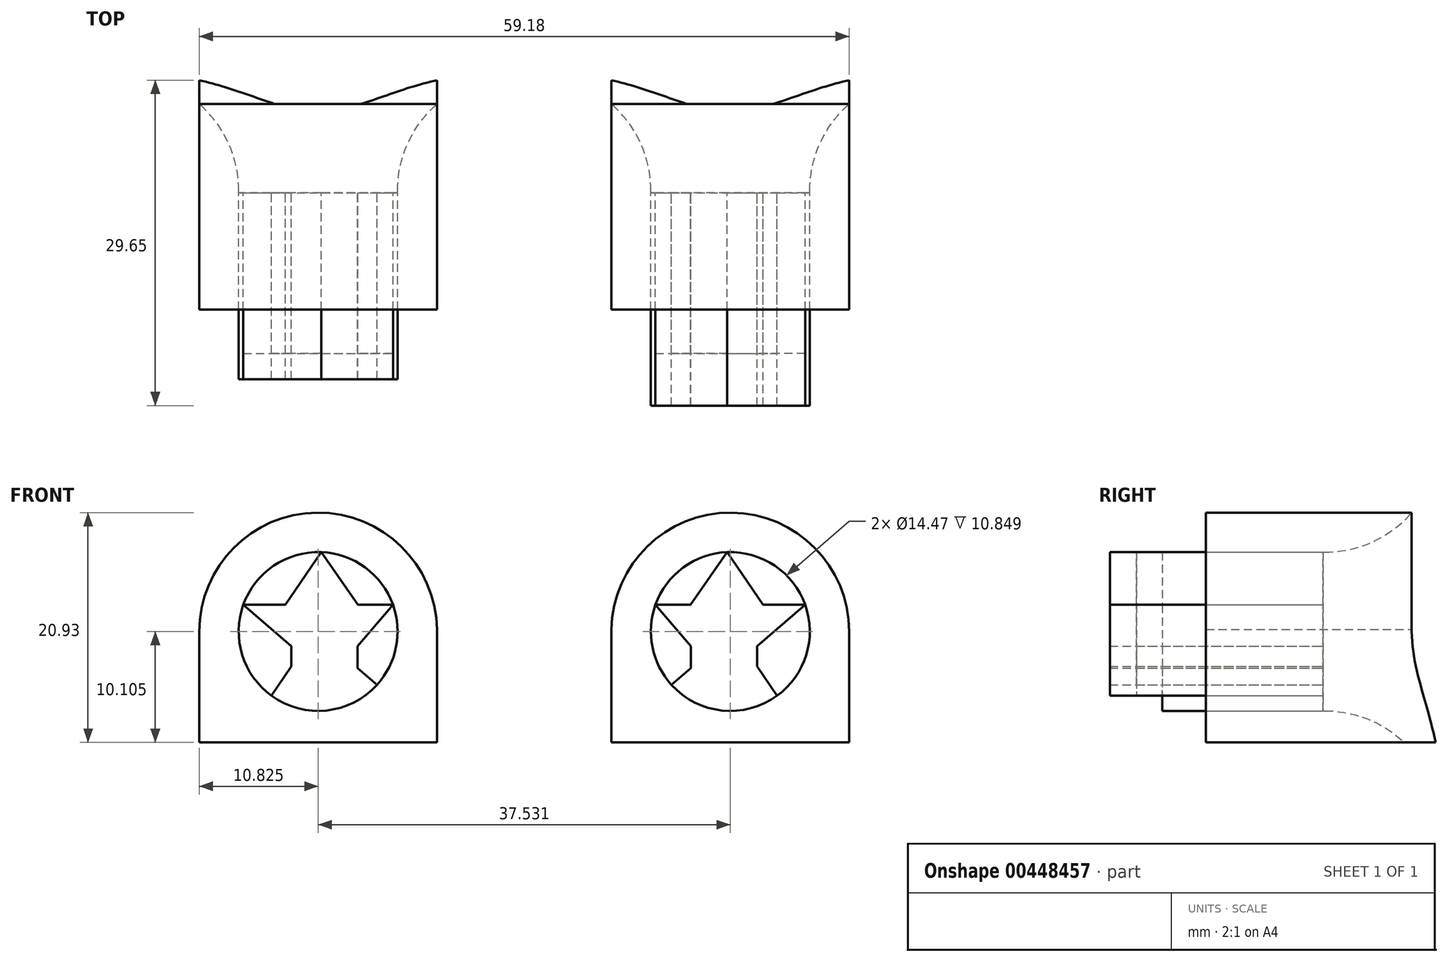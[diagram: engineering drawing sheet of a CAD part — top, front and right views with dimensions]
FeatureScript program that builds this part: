
annotation { "Feature Type Name" : "Feature", "Feature Type Description" : "" }
export const myFeature = defineFeature(function(context is Context, id is Id, definition is map)
    precondition{}
    {
        {
            var Q0;
            Q0=qCreatedBy(makeId("Front.planeOp"),FACE);
            var sketch = newSketch(context, id + "F0", { "sketchPlane" : qUnion([Q0])});
            skLineSegment(sketch, "E0", {"start": v(-29.6, 0) * mm, "end": v(-7.94, 0) * mm});
            skLineSegment(sketch, "E1", {"start": v(-7.94, 0) * mm, "end": v(-7.94, 10.29) * mm});
            skLineSegment(sketch, "E2", {"start": v(-29.6, 0) * mm, "end": v(-29.6, 10.1) * mm});
            skLineSegment(sketch, "E3.MirrorCS", {"start": v(7.94, 0) * mm, "end": v(7.94, 10.29) * mm});
            skLineSegment(sketch, "E4.MirrorCS", {"start": v(29.6, 0) * mm, "end": v(7.94, 0) * mm});
            skLineSegment(sketch, "E5.MirrorCS", {"start": v(29.6, 0) * mm, "end": v(29.6, 10.1) * mm});
            skArc(sketch, "E6", {"start": v(-7.94, 10.29) * mm, "mid": v(-18.86, 20.93) * mm, "end": v(-29.6, 10.1) * mm});
            skArc(sketch, "E7.MirrorCS", {"start": v(7.94, 10.29) * mm, "mid": v(18.86, 20.93) * mm, "end": v(29.6, 10.1) * mm});
            skCircle(sketch, "E8", {"center": v(-18.77, 10.1) * mm, "radius": 7.23 * mm});
            skLineSegment(sketch, "E9", {"start": v(-18.49, 17.33) * mm, "end": v(-21.76, 12.54) * mm});
            skLineSegment(sketch, "E10", {"start": v(-18.49, 17.33) * mm, "end": v(-15.15, 12.54) * mm});
            skLineSegment(sketch, "E11", {"start": v(-15.15, 12.54) * mm, "end": v(-11.95, 12.54) * mm});
            skLineSegment(sketch, "E12", {"start": v(-11.95, 12.54) * mm, "end": v(-15.15, 12.54) * mm});
            skLineSegment(sketch, "E13", {"start": v(-25.58, 12.54) * mm, "end": v(-21.76, 12.54) * mm});
            skLineSegment(sketch, "E14", {"start": v(-11.95, 12.54) * mm, "end": v(-15.19, 8.78) * mm});
            skLineSegment(sketch, "E15", {"start": v(-25.58, 12.54) * mm, "end": v(-21.22, 8.78) * mm});
            skLineSegment(sketch, "E16", {"start": v(-21.22, 8.78) * mm, "end": v(-21.22, 6.93) * mm});
            skLineSegment(sketch, "E17", {"start": v(-15.19, 8.78) * mm, "end": v(-15.19, 6.78) * mm});
            skLineSegment(sketch, "E18", {"start": v(-15.19, 6.78) * mm, "end": v(-13.4, 5.24) * mm});
            skLineSegment(sketch, "E19", {"start": v(-21.22, 6.93) * mm, "end": v(-23, 4.24) * mm});
            skLineSegment(sketch, "E20.MirrorCS", {"start": v(21.22, 6.93) * mm, "end": v(23, 4.24) * mm});
            skLineSegment(sketch, "E21.MirrorCS", {"start": v(18.49, 17.33) * mm, "end": v(15.15, 12.54) * mm});
            skLineSegment(sketch, "E22.MirrorCS", {"start": v(18.49, 17.33) * mm, "end": v(21.76, 12.54) * mm});
            skLineSegment(sketch, "E23.MirrorCS", {"start": v(25.58, 12.54) * mm, "end": v(21.22, 8.78) * mm});
            skLineSegment(sketch, "E24.MirrorCS", {"start": v(25.58, 12.54) * mm, "end": v(21.76, 12.54) * mm});
            skLineSegment(sketch, "E25.MirrorCS", {"start": v(11.95, 12.54) * mm, "end": v(15.15, 12.54) * mm});
            skLineSegment(sketch, "E26.MirrorCS", {"start": v(11.95, 12.54) * mm, "end": v(15.19, 8.78) * mm});
            skLineSegment(sketch, "E27.MirrorCS", {"start": v(15.19, 8.78) * mm, "end": v(15.19, 6.78) * mm});
            skLineSegment(sketch, "E28.MirrorCS", {"start": v(21.22, 8.78) * mm, "end": v(21.22, 6.93) * mm});
            skLineSegment(sketch, "E29.MirrorCS", {"start": v(15.19, 6.78) * mm, "end": v(13.4, 5.24) * mm});
            skCircle(sketch, "E30.MirrorC", {"center": v(18.77, 10.1) * mm, "radius": 7.23 * mm});
            skSolve(sketch);
        }
        {
            var Q0;
            Q0 = qSketchRegion(id + "F0", true);
            extrude(context, id + "F1", {"entities" : qUnion([Q0]), "endBound" : BoundingType.SYMMETRIC, "depth" : 21.3 * mm});
        }
        {
            var Q0;
            Q0=makeQuery(id+"F1.opExtrude","CAP_EDGE",EDGE,{"disambiguationData":[OSD([sQuery(id+"F0.wireOp",EDGE,"E30.MirrorC")])],"isStart":true});
            var Q1;
            Q1=makeQuery(id+"F1.opExtrude","CAP_EDGE",EDGE,{"disambiguationData":[OSD([sQuery(id+"F0.wireOp",EDGE,"E8")])],"isStart":true});
            fillet(context, id + "F2", {"entities" : qUnion([Q0, Q1]), "radius" : 10.46 * mm, "tangentPropagation" : true, "allowEdgeOverflow" : false});
        }
        {
            var Q0;
            Q0=makeQuery(id+"F0.imprint","IMPRINT",FACE,{"disambiguationData":[TD([[makeQuery(id+"F0.imprint","IMPRINT",EDGE,{"derivedFrom":sQuery(id+"F0.wireOp",EDGE,"E9")}),1.0]])]});
            var Q1;
            {var subQ1=sQuery(id+"F0.wireOp",EDGE,"E20.MirrorCS");Q1=makeQuery(id+"F0.imprint","IMPRINT",FACE,{"disambiguationData":[TD([[makeQuery(id+"F0.imprint","IMPRINT",EDGE,{"derivedFrom":subQ1}),-1.0]])]});}
            extrude(context, id + "F3", {"entities" : qUnion([Q0, Q1]), "depth" : 14.63 * mm});
        }
        {
            var Q0;
            {var subQ0=sQuery(id+"F0.wireOp",EDGE,"E9");Q0=makeQuery(id+"F0.imprint","IMPRINT",FACE,{"disambiguationData":[TD([[makeQuery(id+"F0.imprint","IMPRINT",EDGE,{"derivedFrom":subQ0}),-1.0]])]});}
            var Q1;
            {var subQ0=sQuery(id+"F0.wireOp",EDGE,"E10");Q1=makeQuery(id+"F0.imprint","IMPRINT",FACE,{"disambiguationData":[TD([[makeQuery(id+"F0.imprint","IMPRINT",EDGE,{"derivedFrom":subQ0}),1.0]])]});}
            var Q2;
            {var subQ0=sQuery(id+"F0.wireOp",EDGE,"E14");Q2=makeQuery(id+"F0.imprint","IMPRINT",FACE,{"disambiguationData":[TD([[makeQuery(id+"F0.imprint","IMPRINT",EDGE,{"derivedFrom":subQ0}),1.0]])]});}
            var Q3;
            {var subQ0=sQuery(id+"F0.wireOp",EDGE,"E15");Q3=makeQuery(id+"F0.imprint","IMPRINT",FACE,{"disambiguationData":[TD([[makeQuery(id+"F0.imprint","IMPRINT",EDGE,{"derivedFrom":subQ0}),-1.0]])]});}
            extrude(context, id + "F4", {"entities" : qUnion([Q0, Q1, Q2, Q3]), "depth" : 16.98 * mm});
        }
        {
            var Q0;
            {var subQ0=sQuery(id+"F0.wireOp",EDGE,"E26.MirrorCS");Q0=makeQuery(id+"F0.imprint","IMPRINT",FACE,{"disambiguationData":[TD([[makeQuery(id+"F0.imprint","IMPRINT",EDGE,{"derivedFrom":subQ0}),-1.0]])]});}
            var Q1;
            {var subQ0=sQuery(id+"F0.wireOp",EDGE,"E21.MirrorCS");Q1=makeQuery(id+"F0.imprint","IMPRINT",FACE,{"disambiguationData":[TD([[makeQuery(id+"F0.imprint","IMPRINT",EDGE,{"derivedFrom":subQ0}),-1.0]])]});}
            var Q2;
            {var subQ0=sQuery(id+"F0.wireOp",EDGE,"E22.MirrorCS");Q2=makeQuery(id+"F0.imprint","IMPRINT",FACE,{"disambiguationData":[TD([[makeQuery(id+"F0.imprint","IMPRINT",EDGE,{"derivedFrom":subQ0}),1.0]])]});}
            var Q3;
            {var subQ0=sQuery(id+"F0.wireOp",EDGE,"E20.MirrorCS");Q3=makeQuery(id+"F0.imprint","IMPRINT",FACE,{"disambiguationData":[TD([[makeQuery(id+"F0.imprint","IMPRINT",EDGE,{"derivedFrom":subQ0}),1.0]])]});}
            extrude(context, id + "F5", {"entities" : qUnion([Q0, Q1, Q2, Q3]), "depth" : 19.4 * mm});
        }
    });
